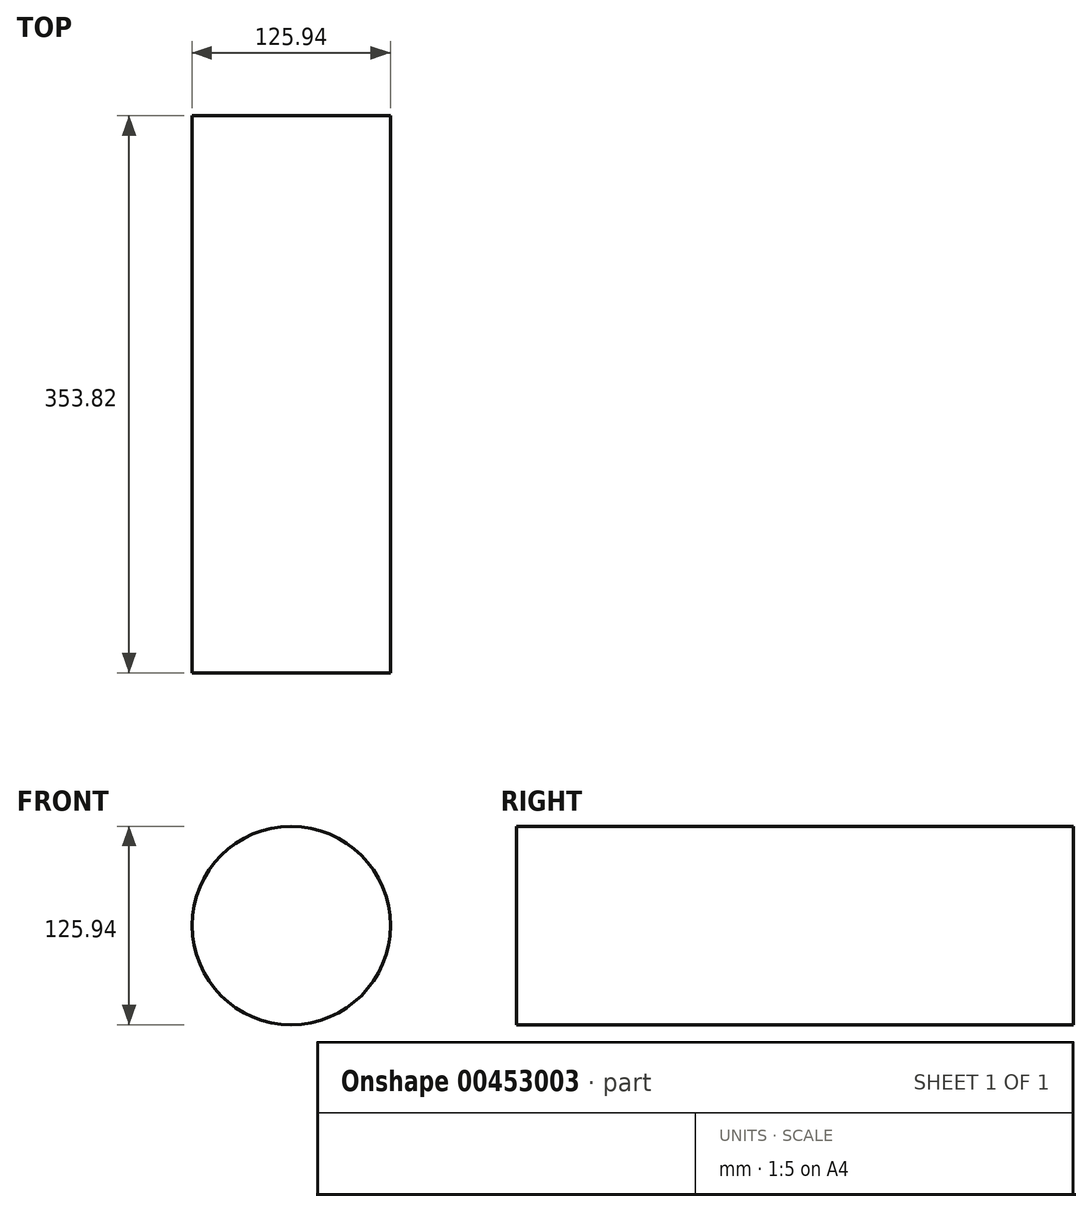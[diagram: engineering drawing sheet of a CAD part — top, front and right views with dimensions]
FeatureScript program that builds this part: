
annotation { "Feature Type Name" : "Feature", "Feature Type Description" : "" }
export const myFeature = defineFeature(function(context is Context, id is Id, definition is map)
    precondition{}
    {
        {
            var Q0;
            Q0=qCreatedBy(makeId("Front.planeOp"),FACE);
            var sketch = newSketch(context, id + "F0", { "sketchPlane" : qUnion([Q0])});
            skCircle(sketch, "E0", {"center": v(0, 0) * mm, "radius": 62.97 * mm});
            skSolve(sketch);
        }
        {
            var Q0;
            Q0=makeQuery(id+"F0.imprint","IMPRINT",FACE,{"disambiguationData":[TD([[makeQuery(id+"F0.imprint","IMPRINT",EDGE,{"derivedFrom":sQuery(id+"F0.wireOp",EDGE,"E0")}),1.0]])]});
            extrude(context, id + "F1", {"entities" : qUnion([Q0]), "depth" : 353.82 * mm});
        }
    });
